# Revit family: CHI_Overhead_MaxSpeed1000_300x180
name_source: partatom
category: Doors
units: mm (PartAtom-declared; Revit-internal decimal feet)

## family parameters
Always vertical = Yes
Classification Number = 23.30.10.00
Cut with Voids When Loaded = No
Host = Wall
Room Calculation Point = No
Shared = No

## types (1)
- CHI_Overhead_MaxSpeed1000_300x180
    Braces = 7
    Construction Details = https://www.arcat.com
    Frame Projection Ext. = 0' - 1"
    Frame Projection Int. = 0' - 1"
    Frame Width = 0' - 3"
    Function = Interior
    Height = 15' - 0"
    Installation-Fabrication = https://performaxglobal.com
    Manufacturer = C.H.I. Overhead Doors
    Manufacturer Fax = 217-543-4454
    Manufacturer Website = https://www.chiohd.com
    Model = MaxSpeed 1000
    Overall Height = 16' - 8"
    Overall Width = 25' - 10"
    Product Data = https://performaxglobal.com
    Sales Information = https://performaxglobal.com
    Specification = https://www.arcat.com
    URL = https://performaxglobal.com
    Wall Closure = By host
    Width = 25' - 0"

## geometry (parser evidence)
native form markers: Sweep x10
no freeform markers — native parametric forms only
